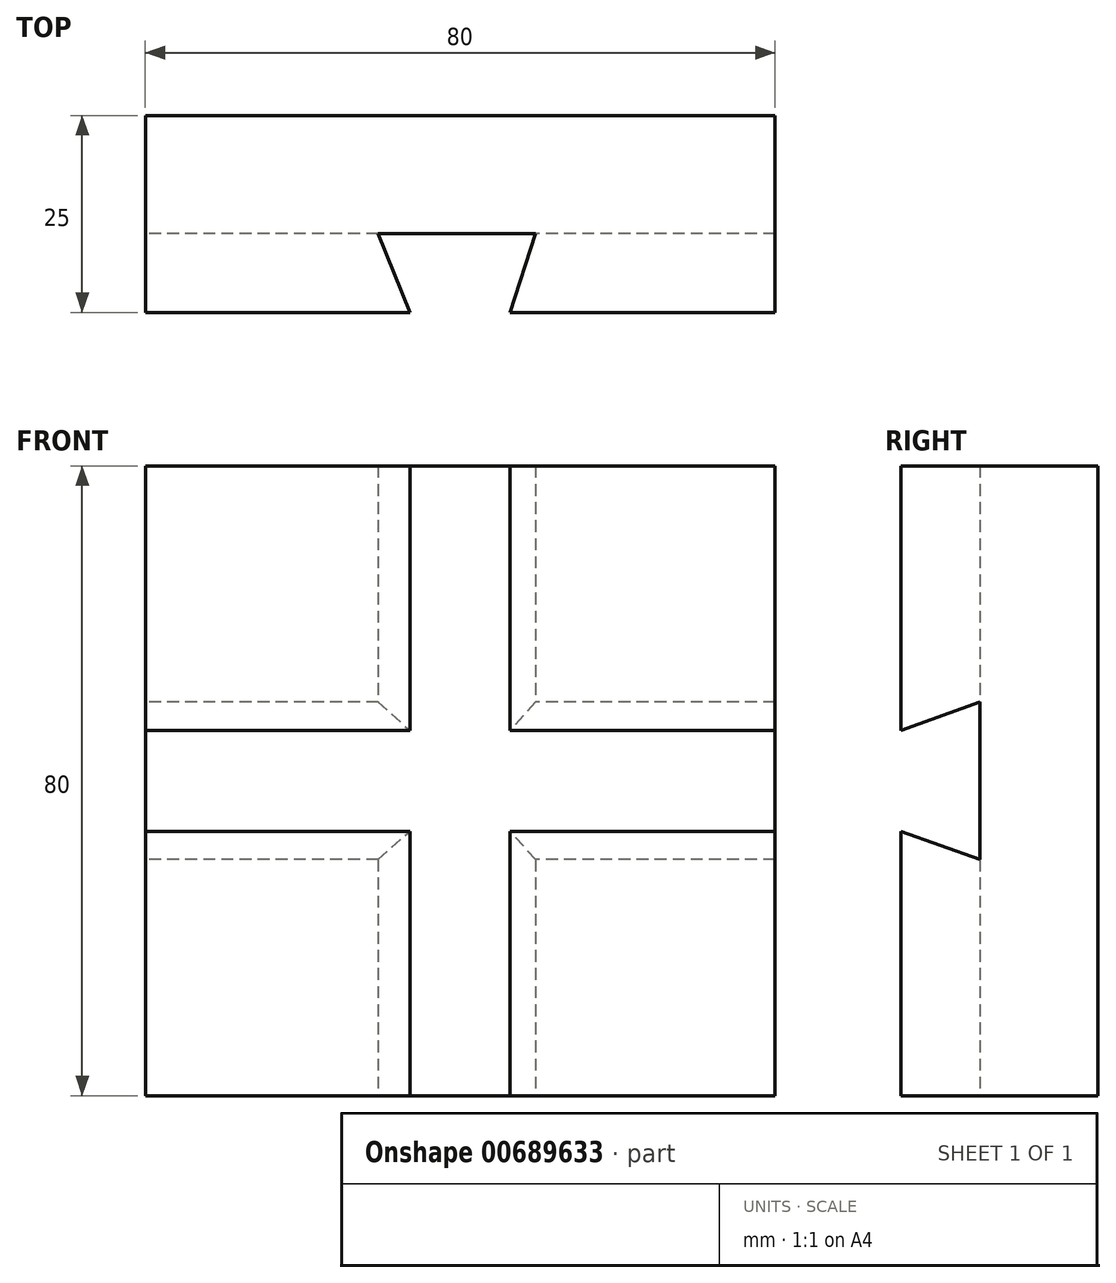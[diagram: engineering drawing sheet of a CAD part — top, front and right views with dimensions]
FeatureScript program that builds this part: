
annotation { "Feature Type Name" : "Feature", "Feature Type Description" : "" }
export const myFeature = defineFeature(function(context is Context, id is Id, definition is map)
    precondition{}
    {
        {
            var Q0;
            Q0=qCreatedBy(makeId("Front.planeOp"),FACE);
            var sketch = newSketch(context, id + "F0", { "sketchPlane" : qUnion([Q0])});
            skLineSegment(sketch, "E0.bottom", {"start": v(-39.58, 46.11) * mm, "end": v(40.42, 46.11) * mm});
            skLineSegment(sketch, "E0.top", {"start": v(-39.58, -33.89) * mm, "end": v(40.42, -33.89) * mm});
            skLineSegment(sketch, "E0.left", {"start": v(-39.58, 46.11) * mm, "end": v(-39.58, -33.89) * mm});
            skLineSegment(sketch, "E0.right", {"start": v(40.42, 46.11) * mm, "end": v(40.42, -33.89) * mm});
            skSolve(sketch);
        }
        {
            var Q0;
            Q0 = qSketchRegion(id + "F0", true);
            extrude(context, id + "F1", {"entities" : qUnion([Q0]), "oppositeDirection" : true, "depth" : 25 * mm, "offsetDistance" : 25 * mm});
        }
        {
            var Q0;
            Q0=makeQuery(id+"F1.opExtrude","SWEPT_FACE",FACE,{"disambiguationData":[OSD([sQuery(id+"F0.wireOp",EDGE,"E0.top")])]});
            var sketch = newSketch(context, id + "F2", { "sketchPlane" : qUnion([Q0])});
            skLineSegment(sketch, "E1", {"start": v(-10, -10) * mm, "end": v(10, -10) * mm});
            skLineSegment(sketch, "E2", {"start": v(-5.97, 0) * mm, "end": v(-10, -10) * mm});
            skLineSegment(sketch, "E3", {"start": v(6.78, 0) * mm, "end": v(10, -10) * mm});
            skSolve(sketch);
        }
        {
            var Q0;
            Q0=makeQuery(id+"F2.imprint","IMPRINT",FACE,{"disambiguationData":[TD([[makeQuery(id+"F2.imprint","IMPRINT",EDGE,{"derivedFrom":sQuery(id+"F2.wireOp",EDGE,"E1")}),1.0]])]});
            extrude(context, id + "F3", {"entities" : qUnion([Q0]), "operationType" : NewBodyOperationType.REMOVE, "oppositeDirection" : true, "depth" : 80 * mm, "offsetDistance" : 25 * mm});
        }
        {
            var Q0;
            Q0=makeQuery(id+"F1.opExtrude","SWEPT_FACE",FACE,{"disambiguationData":[OSD([sQuery(id+"F0.wireOp",EDGE,"E0.left")])]});
            var sketch = newSketch(context, id + "F4", { "sketchPlane" : qUnion([Q0])});
            skLineSegment(sketch, "E4", {"start": v(-10, 6.11) * mm, "end": v(-10, 16.11) * mm});
            skLineSegment(sketch, "E5", {"start": v(-10, 6.11) * mm, "end": v(-10, -3.89) * mm});
            skLineSegment(sketch, "E6", {"start": v(-10, 16.11) * mm, "end": v(0, 12.5) * mm});
            skLineSegment(sketch, "E7", {"start": v(-10, -3.89) * mm, "end": v(0, -0.3) * mm});
            skSolve(sketch);
        }
        {
            var Q0;
            Q0=makeQuery(id+"F4.imprint","IMPRINT",FACE,{"disambiguationData":[TD([[makeQuery(id+"F4.imprint","IMPRINT",EDGE,{"derivedFrom":sQuery(id+"F4.wireOp",EDGE,"E4")}),-1.0]])]});
            extrude(context, id + "F5", {"entities" : qUnion([Q0]), "operationType" : NewBodyOperationType.REMOVE, "oppositeDirection" : true, "depth" : 80 * mm, "offsetDistance" : 25 * mm});
        }
    });
